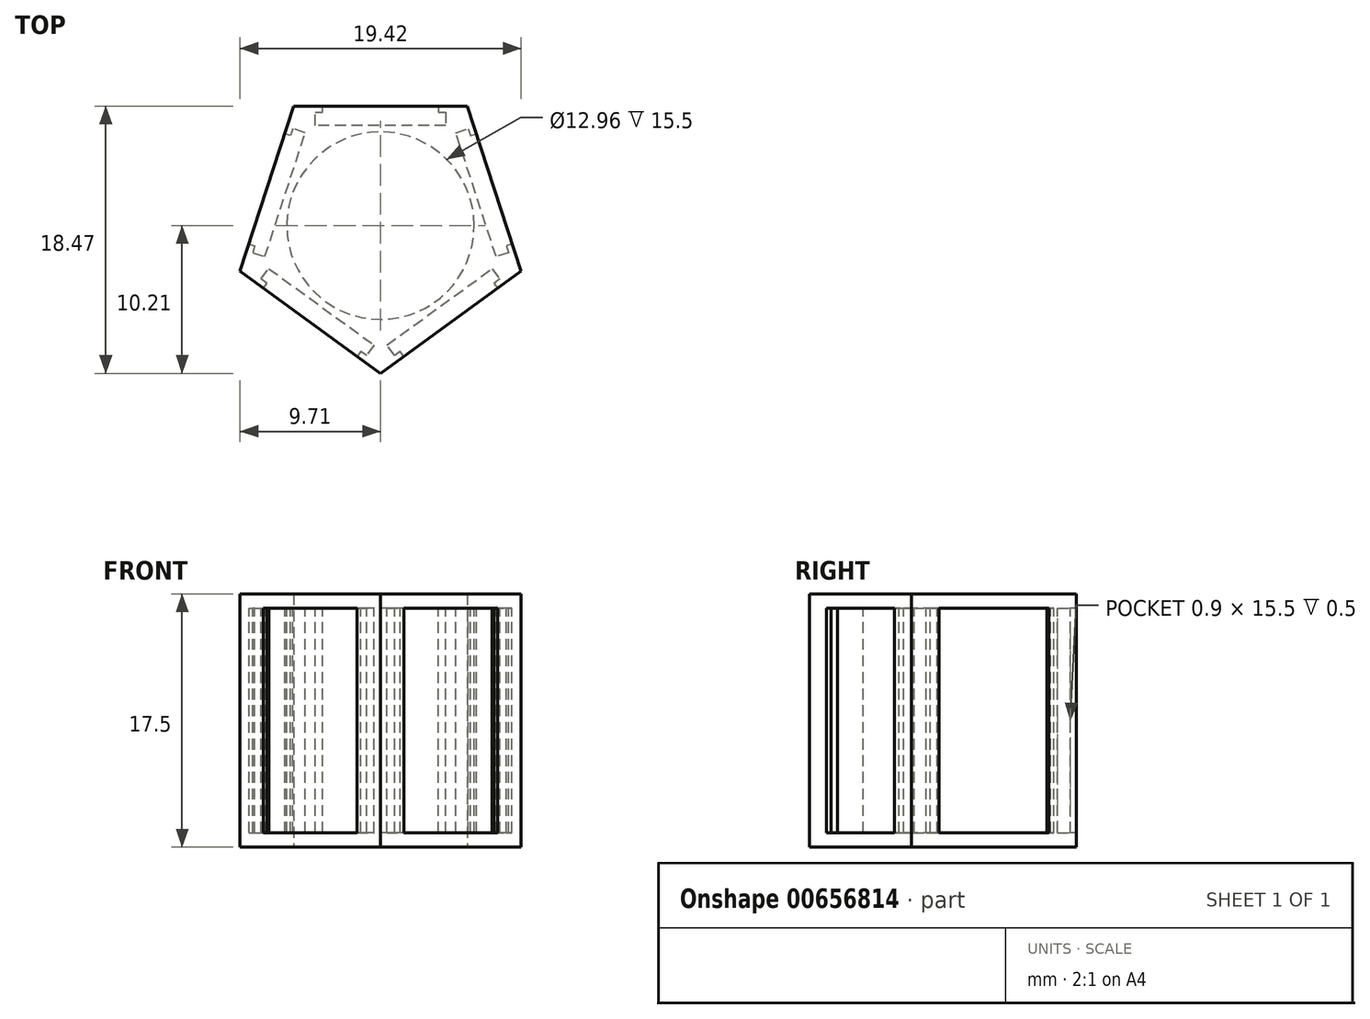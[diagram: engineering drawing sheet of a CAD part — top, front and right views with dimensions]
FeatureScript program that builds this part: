
annotation { "Feature Type Name" : "Feature", "Feature Type Description" : "" }
export const myFeature = defineFeature(function(context is Context, id is Id, definition is map)
    precondition{}
    {
        {
            var Q0;
            Q0=qCreatedBy(makeId("Top.planeOp"),FACE);
            var sketch = newSketch(context, id + "F0", { "sketchPlane" : qUnion([Q0])});
            skCircle(sketch, "E0.cCircle", {"center": v(0, 0) * mm, "radius": 8.26 * mm, "construction": true});
            skLineSegment(sketch, "E0.0", {"start": v(-6, 8.26) * mm, "end": v(6, 8.26) * mm});
            skLineSegment(sketch, "E0.1", {"start": v(6, 8.26) * mm, "end": v(9.7, -3.15) * mm});
            skLineSegment(sketch, "E0.2", {"start": v(9.7, -3.15) * mm, "end": v(0, -10.2) * mm});
            skLineSegment(sketch, "E0.3", {"start": v(0, -10.2) * mm, "end": v(-9.7, -3.15) * mm});
            skLineSegment(sketch, "E0.4", {"start": v(-9.7, -3.15) * mm, "end": v(-6, 8.26) * mm});
            skPoint(sketch, "E0.0.midPoint", {"position": v(0, 8.26) * mm});
            skSolve(sketch);
        }
        {
            var Q0;
            Q0 = qSketchRegion(id + "F0", true);
            extrude(context, id + "F1", {"entities" : qUnion([Q0]), "depth" : 16.5 * mm, "offsetDistance" : 25 * mm});
        }
        {
            var Q0;
            Q0=makeQuery(id+"F1.opExtrude","CAP_FACE",FACE,{"disambiguationData":[OSD([sQuery(id+"F0.wireOp",EDGE,"E0.0"),sQuery(id+"F0.wireOp",EDGE,"E0.1"),sQuery(id+"F0.wireOp",EDGE,"E0.2"),sQuery(id+"F0.wireOp",EDGE,"E0.3"),sQuery(id+"F0.wireOp",EDGE,"E0.4")])],"isStart":false});
            var sketch = newSketch(context, id + "F2", { "sketchPlane" : qUnion([Q0])});
            skLineSegment(sketch, "E1", {"start": v(-8.1, -4.33) * mm, "end": v(-7.84, -4) * mm});
            skLineSegment(sketch, "E2", {"start": v(-7.84, -4) * mm, "end": v(-8.25, -3.7) * mm});
            skLineSegment(sketch, "E3", {"start": v(-8.25, -3.7) * mm, "end": v(-7.72, -2.97) * mm});
            skLineSegment(sketch, "E4", {"start": v(-7.72, -2.97) * mm, "end": v(-0.44, -8.26) * mm});
            skLineSegment(sketch, "E5", {"start": v(-0.44, -8.26) * mm, "end": v(-0.97, -8.99) * mm});
            skLineSegment(sketch, "E6", {"start": v(-0.97, -8.99) * mm, "end": v(-1.37, -8.7) * mm});
            skLineSegment(sketch, "E7", {"start": v(-1.37, -8.7) * mm, "end": v(-1.62, -9.03) * mm});
            skLineSegment(sketch, "E8", {"start": v(-1.62, -9.03) * mm, "end": v(-8.1, -4.33) * mm});
            skLineSegment(sketch, "E9", {"start": v(-9.1, -1.25) * mm, "end": v(-8.7, -1.38) * mm});
            skLineSegment(sketch, "E10", {"start": v(-8.7, -1.38) * mm, "end": v(-8.85, -1.86) * mm});
            skLineSegment(sketch, "E11", {"start": v(-8.85, -1.86) * mm, "end": v(-7.99, -2.14) * mm});
            skLineSegment(sketch, "E12", {"start": v(-7.99, -2.14) * mm, "end": v(-5.2, 6.42) * mm});
            skLineSegment(sketch, "E13", {"start": v(-5.2, 6.42) * mm, "end": v(-6.06, 6.7) * mm});
            skLineSegment(sketch, "E14", {"start": v(-6.06, 6.7) * mm, "end": v(-6.22, 6.23) * mm});
            skLineSegment(sketch, "E15", {"start": v(-6.22, 6.23) * mm, "end": v(-6.62, 6.36) * mm});
            skLineSegment(sketch, "E16", {"start": v(-6.62, 6.36) * mm, "end": v(-9.1, -1.25) * mm});
            skLineSegment(sketch, "E17", {"start": v(8.1, -4.33) * mm, "end": v(1.62, -9.03) * mm});
            skLineSegment(sketch, "E18", {"start": v(1.62, -9.03) * mm, "end": v(1.37, -8.7) * mm});
            skLineSegment(sketch, "E19", {"start": v(1.37, -8.7) * mm, "end": v(0.97, -8.99) * mm});
            skLineSegment(sketch, "E20", {"start": v(0.97, -8.99) * mm, "end": v(0.44, -8.26) * mm});
            skLineSegment(sketch, "E21", {"start": v(0.44, -8.26) * mm, "end": v(7.72, -2.97) * mm});
            skLineSegment(sketch, "E22", {"start": v(7.72, -2.97) * mm, "end": v(8.25, -3.7) * mm});
            skLineSegment(sketch, "E23", {"start": v(8.25, -3.7) * mm, "end": v(7.84, -4) * mm});
            skLineSegment(sketch, "E24", {"start": v(7.84, -4) * mm, "end": v(8.1, -4.33) * mm});
            skLineSegment(sketch, "E25", {"start": v(-4, 8.26) * mm, "end": v(4, 8.26) * mm});
            skLineSegment(sketch, "E26", {"start": v(4, 8.26) * mm, "end": v(4, 7.84) * mm});
            skLineSegment(sketch, "E27", {"start": v(4, 7.84) * mm, "end": v(4.5, 7.84) * mm});
            skLineSegment(sketch, "E28", {"start": v(4.5, 7.84) * mm, "end": v(4.5, 6.94) * mm});
            skLineSegment(sketch, "E29", {"start": v(4.5, 6.94) * mm, "end": v(-4.5, 6.94) * mm});
            skLineSegment(sketch, "E30", {"start": v(-4.5, 6.94) * mm, "end": v(-4.5, 7.84) * mm});
            skLineSegment(sketch, "E31", {"start": v(-4.5, 7.84) * mm, "end": v(-4, 7.84) * mm});
            skLineSegment(sketch, "E32", {"start": v(-4, 7.84) * mm, "end": v(-4, 8.26) * mm});
            skLineSegment(sketch, "E33", {"start": v(6.62, 6.36) * mm, "end": v(9.1, -1.25) * mm});
            skLineSegment(sketch, "E34", {"start": v(9.1, -1.25) * mm, "end": v(8.7, -1.38) * mm});
            skLineSegment(sketch, "E35", {"start": v(8.7, -1.38) * mm, "end": v(8.85, -1.86) * mm});
            skLineSegment(sketch, "E36", {"start": v(8.85, -1.86) * mm, "end": v(7.99, -2.14) * mm});
            skLineSegment(sketch, "E37", {"start": v(7.99, -2.14) * mm, "end": v(5.2, 6.42) * mm});
            skLineSegment(sketch, "E38", {"start": v(5.2, 6.42) * mm, "end": v(6.06, 6.7) * mm});
            skLineSegment(sketch, "E39", {"start": v(6.06, 6.7) * mm, "end": v(6.22, 6.23) * mm});
            skLineSegment(sketch, "E40", {"start": v(6.22, 6.23) * mm, "end": v(6.62, 6.36) * mm});
            skCircle(sketch, "E41", {"center": v(0, 0) * mm, "radius": 6.48 * mm});
            skSolve(sketch);
        }
        {
            var Q0;
            Q0 = qSketchRegion(id + "F2", true);
            extrude(context, id + "F3", {"entities" : qUnion([Q0]), "operationType" : NewBodyOperationType.REMOVE, "oppositeDirection" : true, "depth" : 15.5 * mm, "offsetDistance" : 25 * mm});
        }
        {
            var Q0;
            Q0=makeQuery(id+"F1.opExtrude","CAP_FACE",FACE,{"disambiguationData":[OSD([sQuery(id+"F0.wireOp",EDGE,"E0.0"),sQuery(id+"F0.wireOp",EDGE,"E0.1"),sQuery(id+"F0.wireOp",EDGE,"E0.2"),sQuery(id+"F0.wireOp",EDGE,"E0.3"),sQuery(id+"F0.wireOp",EDGE,"E0.4")])],"isStart":false});
            var sketch = newSketch(context, id + "F4", { "sketchPlane" : qUnion([Q0])});
            skCircle(sketch, "E42.cCircle", {"center": v(0, 0) * mm, "radius": 8.26 * mm, "construction": true});
            skLineSegment(sketch, "E42.0", {"start": v(-6, 8.26) * mm, "end": v(6, 8.26) * mm});
            skLineSegment(sketch, "E42.1", {"start": v(6, 8.26) * mm, "end": v(9.7, -3.15) * mm});
            skLineSegment(sketch, "E42.2", {"start": v(9.7, -3.15) * mm, "end": v(0, -10.2) * mm});
            skLineSegment(sketch, "E42.3", {"start": v(0, -10.2) * mm, "end": v(-9.7, -3.15) * mm});
            skLineSegment(sketch, "E42.4", {"start": v(-9.7, -3.15) * mm, "end": v(-6, 8.26) * mm});
            skPoint(sketch, "E42.0.midPoint", {"position": v(0, 8.26) * mm});
            skSolve(sketch);
        }
        {
            var Q0;
            Q0 = qSketchRegion(id + "F4", true);
            extrude(context, id + "F5", {"entities" : qUnion([Q0]), "operationType" : NewBodyOperationType.ADD, "depth" : 1 * mm, "offsetDistance" : 25 * mm});
        }
        {
            var Q0;
            Q0 = qSketchRegion(id + "F2", true);
            extrude(context, id + "F6", {"entities" : qUnion([Q0]), "operationType" : NewBodyOperationType.REMOVE, "oppositeDirection" : true, "depth" : 15.5 * mm, "offsetDistance" : 25 * mm});
        }
    });
